# Revit family: IS_BlendCurve_T3760_BIM_NL
name_source: partatom
category: Plumbing Fixtures
units: mm (PartAtom-declared; Revit-internal decimal feet)

## family parameters
Always vertical = No
Cut with Voids When Loaded = No
OmniClass Number = 23.45.05.21.11.11
OmniClass Title = Water Operated Water Closets
Part Type = Normal
Room Calculation Point = No
Round Connector Dimension = Use Diameter
Shared = No
Work Plane-Based = No

## types (1)
- T376001 - Blend Curve Wrapover Seat & Cover, Soft Close, Gloss White
    Accesoires = https://www.idealstandard.nl
    Accessories = https://www.idealstandard.nl
    Afmetingen = 360 x 457 x 32 mm
    Afwerking = Wit
    AreaUnits = millimetres
    Artikelnummer = T376001
    Artikelomschrijving = WC-Sitz Blend Curve Softclosing 360x455x35mm Weiß
    Artikelreferentie = WC-Sitz Blend Curve Softclosing 360x455x35mm Weiß
    Auteur = Ideal Standard
    BIMObjectName = IS_IdealStandard_WC seats and covers_BlendCurve_T3760
    BIMobject category = Toilet Seats
    BIMobject category code = sanitary-toilet-seats
    BIMobject main category = Sanitary
    BIMobject main category code = sanitary
    BarCode = 8014140457701
    Barcode = 8014140457701
    Beschrijvinggarantie = Herstellergarantie
    Bestanddelen = WC-Sitz _DESoftclosing 360x455x35mm Weiß
    BimObjectNaam = IS_IdealStandard_WC seats and covers_BlendCurve_T3760
    Brand = Ideal Standard
    Brand url = https://www.idealstandard.nl
    Breedte = 0
    BrutoGewicht = 0
    Color = White
    ConnectionType = Plumbing
    Cost = 0 $
    CurrencyUnit = €
    CurrentRevision = 1
    Date of publishing = 30/04/2021
    Description = Blend Curve Wrapover Seat & Cover, Soft Close, Gloss White
    Diepte = 456 mm
    DurationUnit = Years
    DuurEenheid = Jahre
    Edition number = 1
    Eigenschappen = WC-Sitz Blend Curve Softclosing 360x455x35mm Weiß
    ExpectedLife = 99
    Features = Wrapover Seat & Cover with Soft Close function in Glossy White Finish
    Finish = White
    GTIN code = https://8014140457701
    Garantieunits = Jahre
    GemaaktOp = 26/04/2021
    Help = https://www.idealstandard.nl
    Hoogte = 31.5024100607767
    Hulp = https://www.idealstandard.nl
    IFC Classification = Sanitary Terminal
    IfcExportAs = IfcSanitaryTerminalType
    IfcExportType = WCSEAT
    Installatieinstructies = https://www.idealstandard.nl
    Installation instructions = https://www.idealstandard.nl
    InstallationInstructions = https://www.idealstandard.nl
    Kleur = Weiß
    Lengte = 0 mm  [stored 0 ft]
    LinearUnits = millimetres
    MainColor = White
    MaintenanceInformation = https://www.idealstandard.nl
    Manufacturer = Ideal Standard Nederland BV
    Manufacturer name = Ideal Standard
    ManufacturerURL = https://www.idealstandard.nl
    Masterformat 2014 Code = 10 28 13
    Masterformat 2014 Description = Toilet Accessories
    Materiaal = Acryl
    Material = Acrylic
    Material main = Acrylic
    Merk = Ideal Standard
    Model = T376001
    ModelNumber = T376001
    ModelReference = Blend Curve Wrapover Seat & Cover, Soft Close, Gloss White
    Montageinstuctie = https://www.idealstandard.nl
    NBS Reference Code = 45-35-70/391
    NBS Reference Description = Wc Seats And Covers
    Name = WC seats and covers_BlendCurve_T3760_IdealStandard
    NettWeight = 2.38
    Nettogewicht = 2.38
    NominalDepth = 456 mm
    NominalHeight = 32 mm
    NominalWidth = 361 mm
    Normen = WC seats and covers_BlendCurve_T3760_IdealStandard
    OmniClass Code = 23-31 19 19 17
    OmniClass Description = Water Closet Seats
    OppervlakteEenheid = Millimeter
    Overloop = 0 mm  [stored 0 ft]
    PredefinedType = WC Seats & Covers
    Product Guid = 75b977b7-5843-4c7e-86b7-45c9f7b604c8
    Product SKU = T3760
    Product certification = https://www.idealstandard.nl
    Product data url = https://bimobject.com
    Product family = Blend Cube
    Product group = WC Seats
    Product name = Blend Curve soft close seat & cover
    Product url = https://www.idealstandard.nl
    ProductInformation = https://www.idealstandard.nl
    ProductSoort = Sanitärartikel
    Productinformatie = https://www.idealstandard.nl
    QR code = http://bimobject.com
    Referentie = T376001
    Revisie = 1
    SeatColor = White
    SeatHasCover = Yes
    SeatMaterial = Acrylics
    SeatType = Soft Close
    Shape = Rectangular
    Size = 360 x 457 x 32 mm
    Space = Internal
    SpareParts = https://www.idealstandard.nl
    Technical description = https://www.idealstandard.nl
    Telefoonnummer = 0049 228 5210
    Typeconnectie = Installation
    UNSPSC Code = 30181505
    URL = https://www.idealstandard.nl
    Uniclass 1.4 Code = L72163
    Uniclass 1.4 Description = Pans, seats
    Uniclass 2.0 Code = PR-35-93-95
    Uniclass 2.0 Description = Wc Seats And Covers
    Uniclass 2015 Code = Pr_40_20_93_95
    Uniclass 2015 Name = WC seats and covers
    Uniclass2015Version = v1.20
    Uniformat II Code = D2010
    Uniformat II Description = Plumbing Fixtures
    Urlproducent = https://www.idealstandard.nl
    ValutaEenheid = €
    Versie = 1
    Version = 1
    Vervangingskosten = 0
    VolumeUnits = Liters
    Volumeunits = Liter
    Vorm = Rechteckig
    WRASURL = https://www.wrasapprovals.co.uk
    WarrantyDescription = Manufacturer Warranty
    WarrantyDurationParts = 99
    WarrantyDurationUnit = Years
    Wisselstukken = https://www.idealstandard.nl
    Youtube clip = https://www.youtube.com

note: [stored X ft] marks values corroborated as IEEE doubles in the binary element streams (Revit-internal decimal feet)

## geometry (parser evidence)
native form markers: Blend x29, Sweep x3
no freeform markers — native parametric forms only
